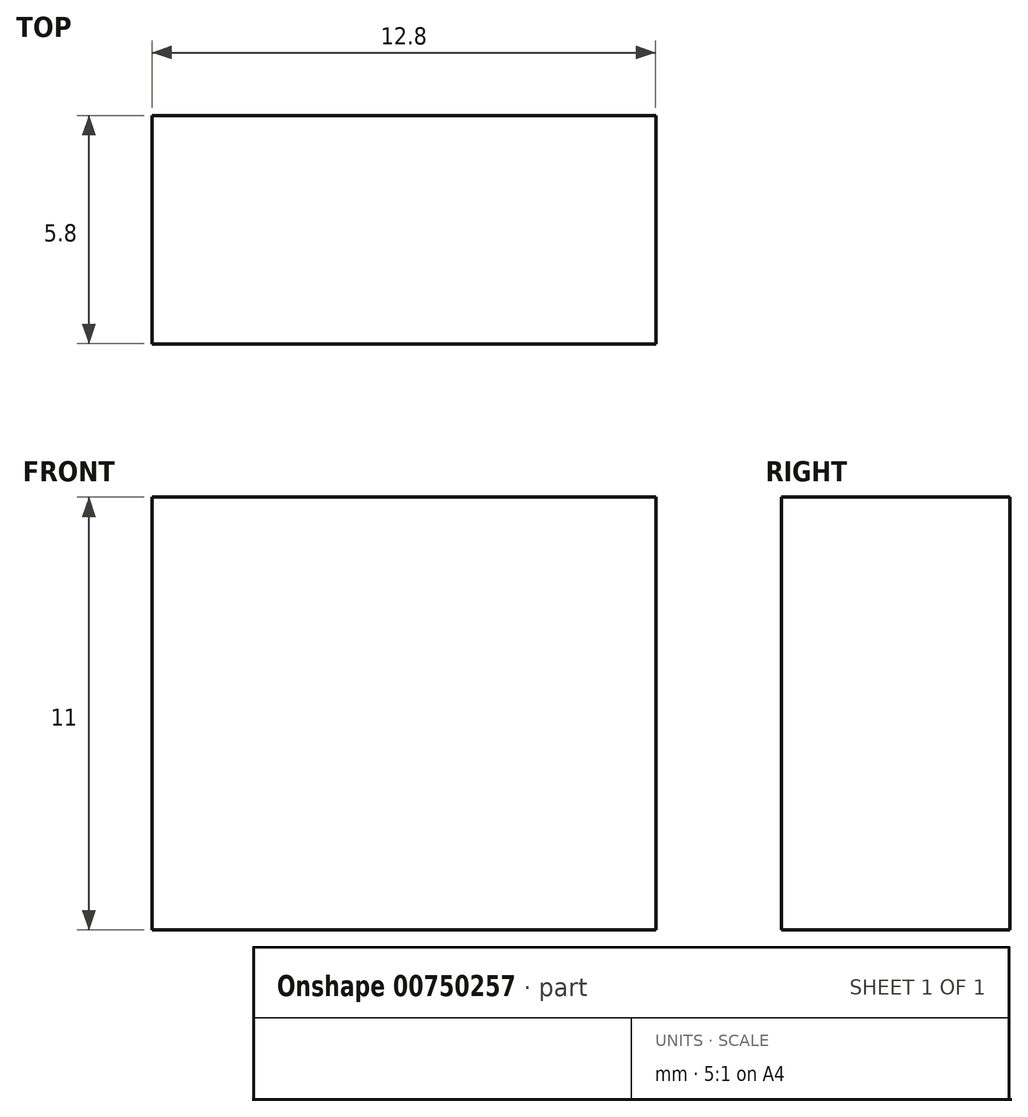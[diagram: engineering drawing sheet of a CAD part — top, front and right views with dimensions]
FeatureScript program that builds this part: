
annotation { "Feature Type Name" : "Feature", "Feature Type Description" : "" }
export const myFeature = defineFeature(function(context is Context, id is Id, definition is map)
    precondition{}
    {
        {
            var Q0;
            Q0=qCreatedBy(makeId("Top.planeOp"),FACE);
            var sketch = newSketch(context, id + "F0", { "sketchPlane" : qUnion([Q0])});
            skLineSegment(sketch, "E0.bottom", {"start": v(-30.75, -6.3) * mm, "end": v(-17.95, -6.3) * mm});
            skLineSegment(sketch, "E0.top", {"start": v(-30.75, -12.1) * mm, "end": v(-17.95, -12.1) * mm});
            skLineSegment(sketch, "E0.left", {"start": v(-30.75, -6.3) * mm, "end": v(-30.75, -12.1) * mm});
            skLineSegment(sketch, "E0.right", {"start": v(-17.95, -6.3) * mm, "end": v(-17.95, -12.1) * mm});
            skSolve(sketch);
        }
        {
            var Q0;
            Q0 = qSketchRegion(id + "F0", true);
            extrude(context, id + "F1", {"entities" : qUnion([Q0]), "depth" : 11 * mm, "offsetDistance" : 25 * mm});
        }
    });
